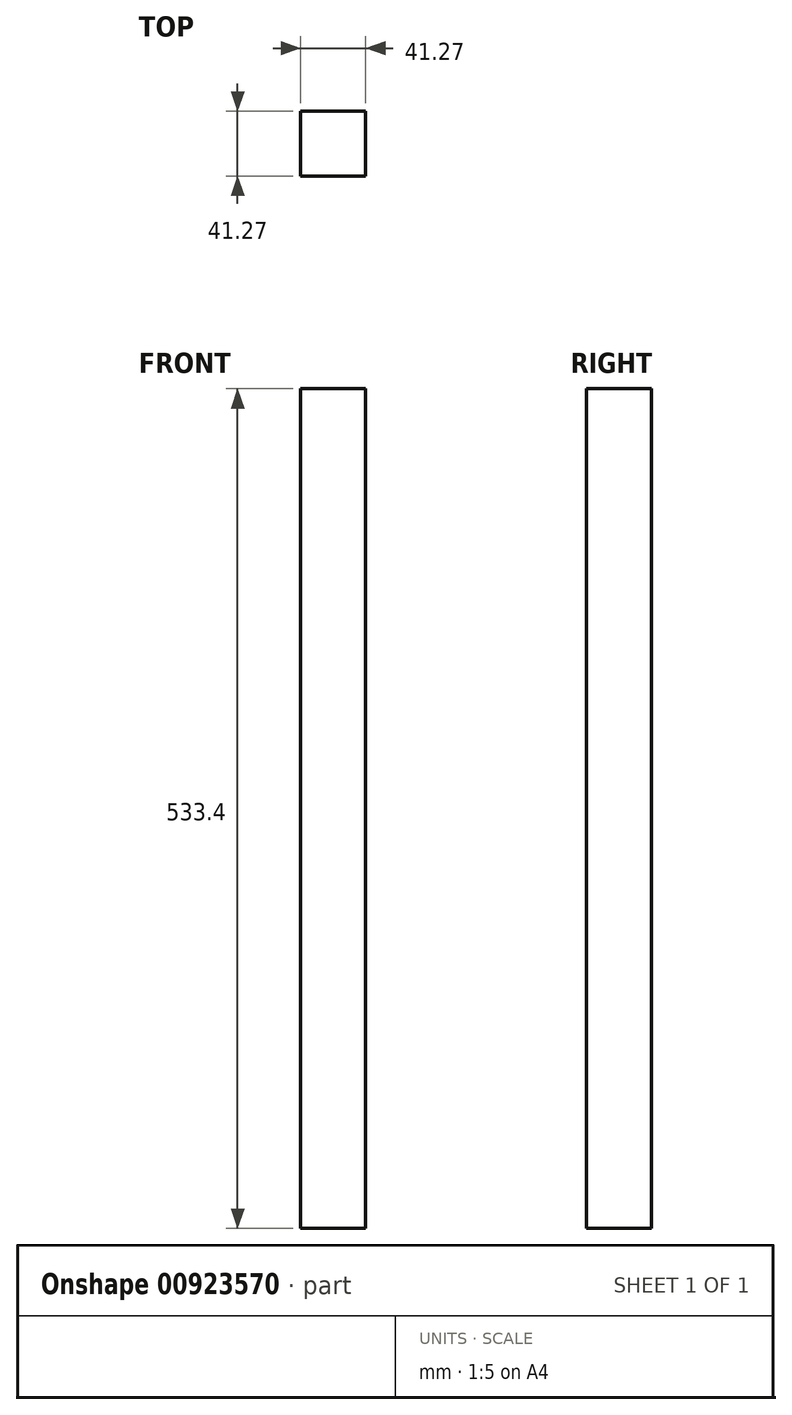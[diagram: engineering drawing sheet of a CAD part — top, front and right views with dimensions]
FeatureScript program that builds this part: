
annotation { "Feature Type Name" : "Feature", "Feature Type Description" : "" }
export const myFeature = defineFeature(function(context is Context, id is Id, definition is map)
    precondition{}
    {
        {
            var Q0;
            Q0=qCreatedBy(makeId("Front.planeOp"),FACE);
            var sketch = newSketch(context, id + "F0", { "sketchPlane" : qUnion([Q0])});
            skLineSegment(sketch, "E0.bottom", {"start": v(0, 0) * mm, "end": v(41.28, 0) * mm});
            skLineSegment(sketch, "E0.top", {"start": v(0, 533.4) * mm, "end": v(41.27, 533.4) * mm});
            skLineSegment(sketch, "E0.left", {"start": v(0, 0) * mm, "end": v(0, 533.4) * mm});
            skLineSegment(sketch, "E0.right", {"start": v(41.28, 0) * mm, "end": v(41.27, 533.4) * mm});
            skSolve(sketch);
        }
        {
            var Q0;
            Q0=makeQuery(id+"F0.imprint","IMPRINT",FACE,{"disambiguationData":[TD([[makeQuery(id+"F0.imprint","IMPRINT",EDGE,{"derivedFrom":sQuery(id+"F0.wireOp",EDGE,"E0.bottom")}),1.0]])]});
            extrude(context, id + "F1", {"entities" : qUnion([Q0]), "depth" : 41.27 * mm, "offsetDistance" : 25.4 * mm});
        }
    });
